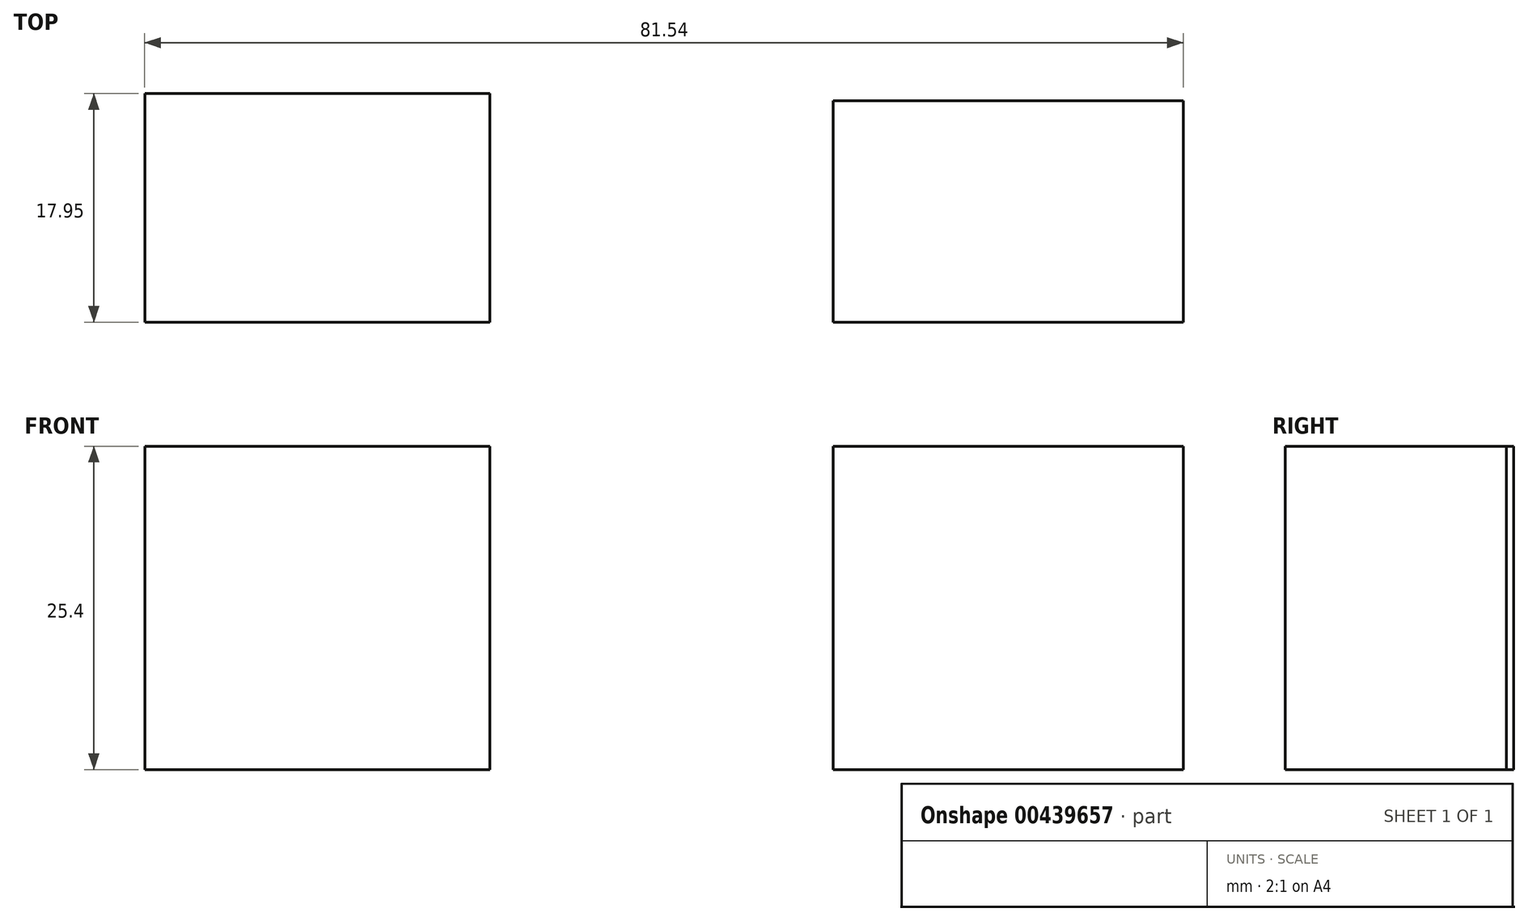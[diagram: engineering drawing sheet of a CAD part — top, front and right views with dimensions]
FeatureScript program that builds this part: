
annotation { "Feature Type Name" : "Feature", "Feature Type Description" : "" }
export const myFeature = defineFeature(function(context is Context, id is Id, definition is map)
    precondition{}
    {
        {
            var Q0;
            Q0=qCreatedBy(makeId("Top.planeOp"),FACE);
            var sketch = newSketch(context, id + "F0", { "sketchPlane" : qUnion([Q0])});
            skLineSegment(sketch, "E0.bottom", {"start": v(-57.86, 56.71) * mm, "end": v(-30.74, 56.71) * mm});
            skLineSegment(sketch, "E0.top", {"start": v(-57.86, 38.76) * mm, "end": v(-30.74, 38.76) * mm});
            skLineSegment(sketch, "E0.left", {"start": v(-57.86, 56.71) * mm, "end": v(-57.86, 38.76) * mm});
            skLineSegment(sketch, "E0.right", {"start": v(-30.74, 56.71) * mm, "end": v(-30.74, 38.76) * mm});
            skLineSegment(sketch, "E1.bottom", {"start": v(-3.82, 56.14) * mm, "end": v(23.68, 56.14) * mm});
            skLineSegment(sketch, "E1.top", {"start": v(-3.82, 38.76) * mm, "end": v(23.68, 38.76) * mm});
            skLineSegment(sketch, "E1.left", {"start": v(-3.82, 56.14) * mm, "end": v(-3.82, 38.76) * mm});
            skLineSegment(sketch, "E1.right", {"start": v(23.68, 56.14) * mm, "end": v(23.68, 38.76) * mm});
            skSolve(sketch);
        }
        {
            var Q0;
            Q0=makeQuery(id+"F0.imprint","IMPRINT",FACE,{"disambiguationData":[TD([[makeQuery(id+"F0.imprint","IMPRINT",EDGE,{"derivedFrom":sQuery(id+"F0.wireOp",EDGE,"E1.bottom")}),-1.0]])]});
            var Q1;
            Q1=makeQuery(id+"F0.imprint","IMPRINT",FACE,{"disambiguationData":[TD([[makeQuery(id+"F0.imprint","IMPRINT",EDGE,{"derivedFrom":sQuery(id+"F0.wireOp",EDGE,"E0.bottom")}),-1.0]])]});
            extrude(context, id + "F1", {"entities" : qUnion([Q0, Q1]), "depth" : 25.4 * mm});
        }
    });
